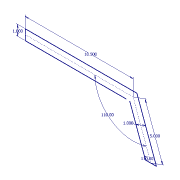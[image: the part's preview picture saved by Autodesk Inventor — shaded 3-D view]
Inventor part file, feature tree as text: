
AUTODESK INVENTOR PART (.ipt)
format: ipt  version: 2012 (Build 160160000, 160)  size: 103,936 bytes
history: native  units: in
note: dims shown in document units (in); Inventor stores cm internally (conversion verified against a paired STEP export)
features: extrude x2, sketch x2, shell x1, fillet x1
ambient origin geometry x8: Origin, YZ Plane, XZ Plane, XY Plane, X Axis, Y Axis, Z Axis, Center Point
feature tree (6):
  extrude  "Extrusion3"  Depth=0.7559in
  shell  "Shell3"  Thickness=10.5in
  extrude  "Extrusion4"  Depth=0.7559in
  fillet  "Fillet2"  Radius=1.0in
  sketch  "Sketch1"  dims[d4=1.0in d5=0.7559in d6=10.5in]
  sketch  "Sketch4"  dims[d7=5.0in d17=0.7559in d18=1.0in d19=1.0in d20=0.0in d21=0.25in d22=0.5in d23=0.5in d24=0.0625in d25=1.0in d26=0.0in d27=0.5in]
